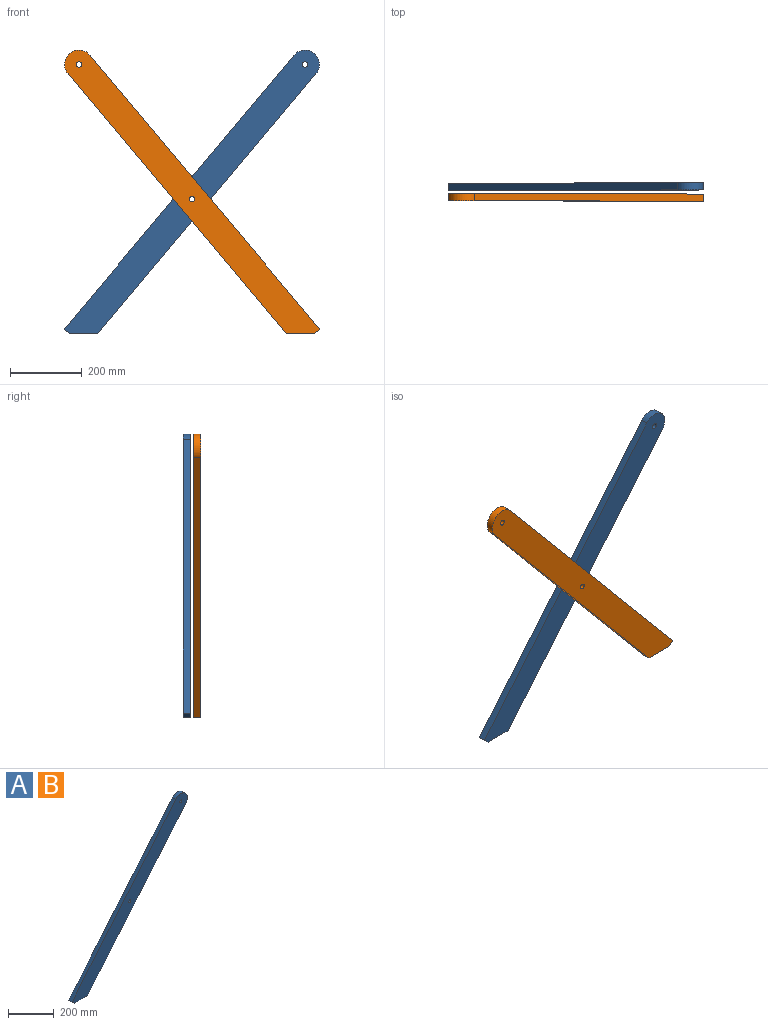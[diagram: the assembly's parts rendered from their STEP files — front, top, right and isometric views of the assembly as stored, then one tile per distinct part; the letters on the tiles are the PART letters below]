
ASSEMBLY  parts=2 mates=1
PART A: 9 faces, bbox 710.8x20x790 mm
  f0: plane 78.32x20mm, normal (0,0,-1), area 1566.5mm2, adj f1,f6,f7,f8
  f1: plane 724.29x607.75mm, normal (0.77,0,-0.64), area 18909.8mm2, adj f0,f2,f7,f8
  f2: cylinder r=40mm len=70.64mm, axis (0,1,0), area 2513.3mm2, adj f1,f3,f7,f8
  f3: plane 762.86x640.11mm, normal (-0.77,0,0.64), area 19916.7mm2, adj f2,f6,f7,f8
  f4: cylinder r=7.5mm len=20mm, axis (0,1,0), area 942.5mm2, adj f7,f8
  f5: cylinder r=7.5mm len=20mm, axis (0,1,0), area 942.5mm2, adj f7,f8
  f6: plane 20x15.32mm, normal (-0.64,0,-0.77), area 400mm2, adj f0,f3,f7,f8
  f7: plane 790x710.75mm, normal (0,-1,0), area 80316.5mm2, adj f0,f1,f2,f3,f4,f5,f6
  f8: plane 790x710.75mm, normal (0,1,0), area 80316.5mm2, adj f0,f1,f2,f3,f4,f5,f6
PART B: same geometry as A
PLACE A t=(-262.45,0,-375)mm
PLACE B rot(axis=(0,0,1),180deg) t=(262.45,-50,-375)mm
MATE revolute B.f5 <-> A.f5  axis (0,1,0) through (0,-30,0)mm
